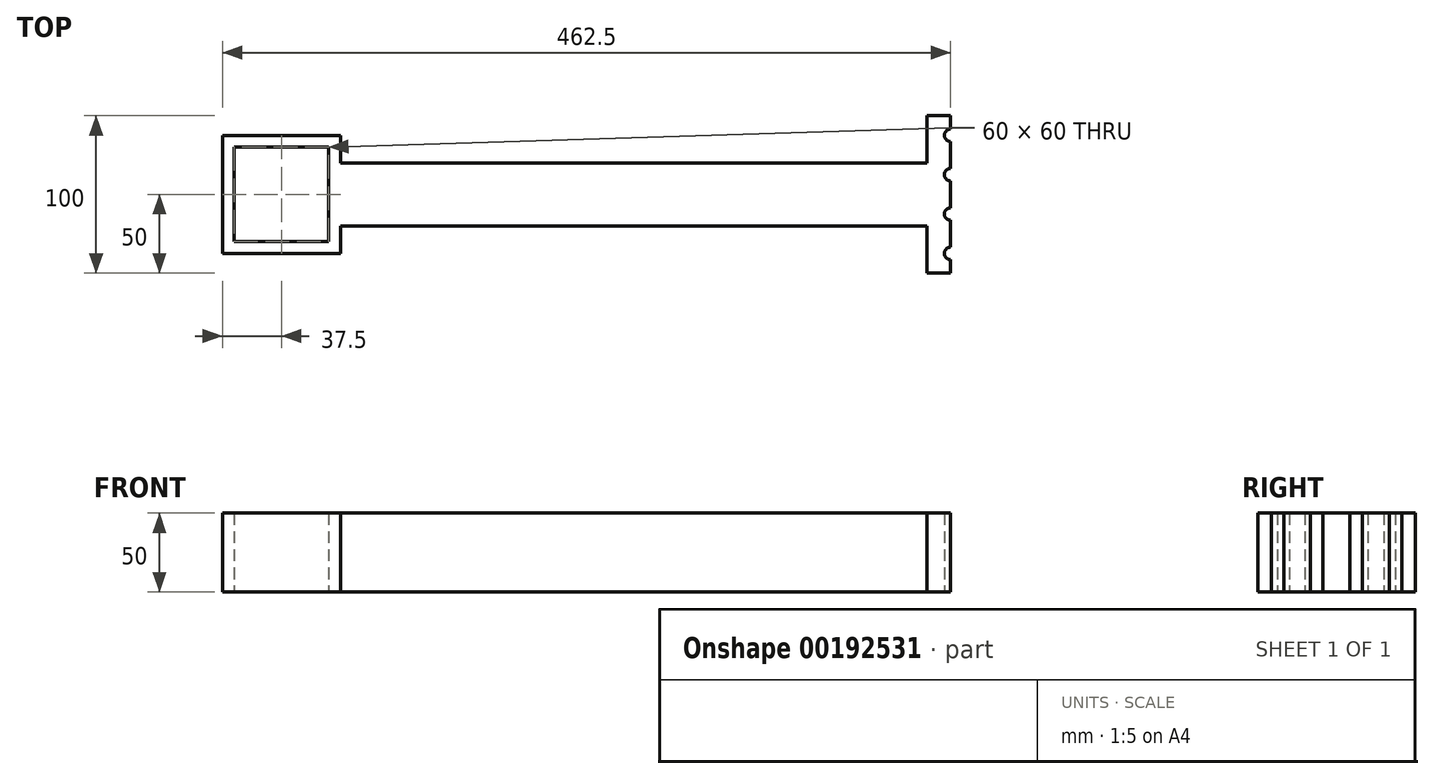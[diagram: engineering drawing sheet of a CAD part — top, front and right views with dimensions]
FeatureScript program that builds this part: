
annotation { "Feature Type Name" : "Feature", "Feature Type Description" : "" }
export const myFeature = defineFeature(function(context is Context, id is Id, definition is map)
    precondition{}
    {
        {
            var Q0;
            Q0=qCreatedBy(makeId("Top.planeOp"),FACE);
            var sketch = newSketch(context, id + "F0", { "sketchPlane" : qUnion([Q0])});
            skLineSegment(sketch, "E0.bottom", {"start": v(37.5, 37.5) * mm, "end": v(-37.5, 37.5) * mm});
            skLineSegment(sketch, "E0.top", {"start": v(37.5, -37.5) * mm, "end": v(-37.5, -37.5) * mm});
            skLineSegment(sketch, "E0.left", {"start": v(37.5, 37.5) * mm, "end": v(37.5, 20) * mm});
            skLineSegment(sketch, "E0.right", {"start": v(-37.5, 37.5) * mm, "end": v(-37.5, -37.5) * mm});
            skPoint(sketch, "E0.middle", {"position": v(0, 0) * mm});
            skLineSegment(sketch, "E1.bottom", {"start": v(30, 30) * mm, "end": v(-30, 30) * mm});
            skLineSegment(sketch, "E1.top", {"start": v(30, -30) * mm, "end": v(-30, -30) * mm});
            skLineSegment(sketch, "E1.left", {"start": v(30, 30) * mm, "end": v(30, -30) * mm});
            skLineSegment(sketch, "E1.right", {"start": v(-30, 30) * mm, "end": v(-30, -30) * mm});
            skLineSegment(sketch, "E2", {"start": v(37.5, 20) * mm, "end": v(410, 20) * mm});
            skLineSegment(sketch, "E3", {"start": v(410, 20) * mm, "end": v(410, 50) * mm});
            skLineSegment(sketch, "E4", {"start": v(410, 50) * mm, "end": v(425, 50) * mm});
            skLineSegment(sketch, "E5", {"start": v(425, 50) * mm, "end": v(425, 41.45) * mm});
            skLineSegment(sketch, "E6", {"start": v(-181.45, 0) * mm, "end": v(167.9, 0) * mm, "construction": true});
            skLineSegment(sketch, "E7.MirrorCS", {"start": v(37.5, -20) * mm, "end": v(410, -20) * mm});
            skLineSegment(sketch, "E8.MirrorCS", {"start": v(410, -20) * mm, "end": v(410, -50) * mm});
            skLineSegment(sketch, "E9.MirrorCS", {"start": v(410, -50) * mm, "end": v(425, -50) * mm});
            skLineSegment(sketch, "E10.MirrorCS", {"start": v(425, -50) * mm, "end": v(425, -41.45) * mm});
            skLineSegment(sketch, "E11.trimOffspring", {"start": v(37.5, -20) * mm, "end": v(37.5, -37.5) * mm});
            skArc(sketch, "E12", {"start": v(425, 41.45) * mm, "mid": v(421.05, 37.5) * mm, "end": v(425, 33.55) * mm});
            skArc(sketch, "E13.0.1.0", {"start": v(425, 16.45) * mm, "mid": v(421.05, 12.5) * mm, "end": v(425, 8.55) * mm});
            skArc(sketch, "E13.0.2.0", {"start": v(425, -8.55) * mm, "mid": v(421.05, -12.5) * mm, "end": v(425, -16.45) * mm});
            skArc(sketch, "E13.0.3.0", {"start": v(425, -33.55) * mm, "mid": v(421.05, -37.5) * mm, "end": v(425, -41.45) * mm});
            skArc(sketch, "E13.1.1.0", {"start": v(425, 16.45) * mm, "mid": v(421.05, 12.5) * mm, "end": v(425, 8.55) * mm});
            skArc(sketch, "E13.1.2.0", {"start": v(425, -8.55) * mm, "mid": v(421.05, -12.5) * mm, "end": v(425, -16.45) * mm});
            skArc(sketch, "E13.1.3.0", {"start": v(425, -33.55) * mm, "mid": v(421.05, -37.5) * mm, "end": v(425, -41.45) * mm});
            skArc(sketch, "E13.2.1.0", {"start": v(425, 16.45) * mm, "mid": v(421.05, 12.5) * mm, "end": v(425, 8.55) * mm});
            skArc(sketch, "E13.2.2.0", {"start": v(425, -8.55) * mm, "mid": v(421.05, -12.5) * mm, "end": v(425, -16.45) * mm});
            skArc(sketch, "E13.2.3.0", {"start": v(425, -33.55) * mm, "mid": v(421.05, -37.5) * mm, "end": v(425, -41.45) * mm});
            skLineSegment(sketch, "E13.direction1", {"start": v(425, 33.55) * mm, "end": v(425, 33.55) * mm});
            skLineSegment(sketch, "E13.direction2", {"start": v(425, 33.55) * mm, "end": v(425, 16.45) * mm, "construction": true});
            skLineSegment(sketch, "E14.trimOffspring", {"start": v(425, 33.55) * mm, "end": v(425, 16.45) * mm});
            skLineSegment(sketch, "E15.trimOffspring", {"start": v(425, 8.55) * mm, "end": v(425, 0) * mm});
            skLineSegment(sketch, "E16.trimOffspring", {"start": v(425, -8.55) * mm, "end": v(425, 0) * mm});
            skLineSegment(sketch, "E17.trimOffspring", {"start": v(425, -33.55) * mm, "end": v(425, -16.45) * mm});
            skSolve(sketch);
        }
        {
            var Q0;
            Q0 = qSketchRegion(id + "F0", true);
            extrude(context, id + "F1", {"entities" : qUnion([Q0]), "endBound" : BoundingType.SYMMETRIC, "depth" : 50 * mm});
        }
    });
